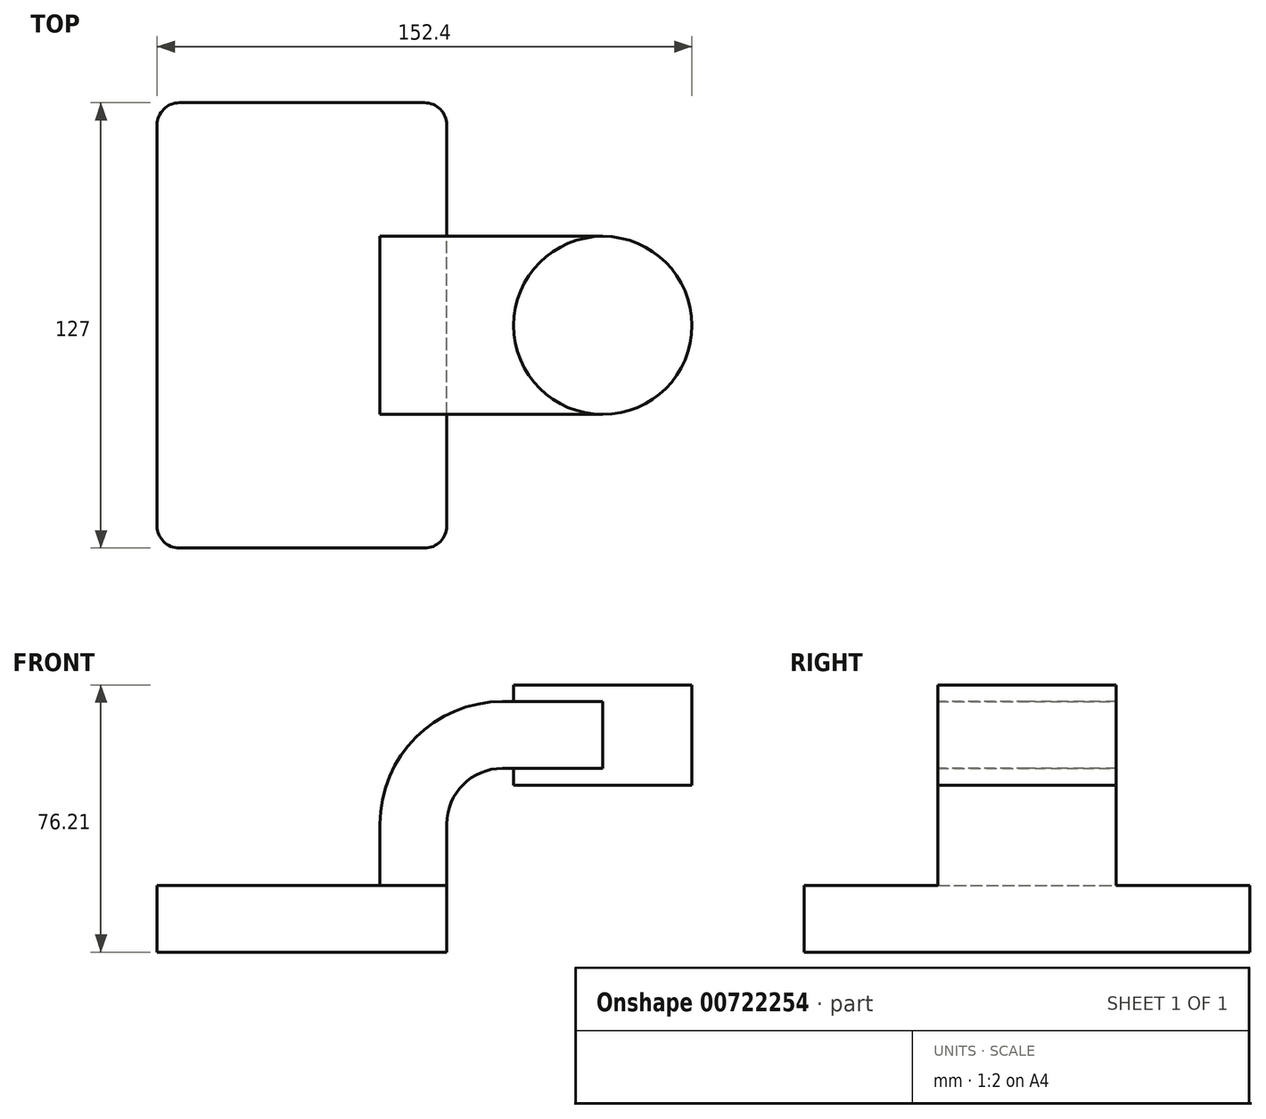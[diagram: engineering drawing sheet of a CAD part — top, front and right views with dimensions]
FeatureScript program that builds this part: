
annotation { "Feature Type Name" : "Feature", "Feature Type Description" : "" }
export const myFeature = defineFeature(function(context is Context, id is Id, definition is map)
    precondition{}
    {
        {
            var Q0;
            Q0=qCreatedBy(makeId("Front.planeOp"),FACE);
            var sketch = newSketch(context, id + "F0", { "sketchPlane" : qUnion([Q0])});
            skLineSegment(sketch, "E0.bottom", {"start": v(-41.28, 9.52) * mm, "end": v(41.28, 9.52) * mm});
            skLineSegment(sketch, "E0.top", {"start": v(-41.28, -9.52) * mm, "end": v(41.28, -9.52) * mm});
            skLineSegment(sketch, "E0.left", {"start": v(-41.28, 9.52) * mm, "end": v(-41.28, -9.52) * mm});
            skLineSegment(sketch, "E0.right", {"start": v(41.28, 9.52) * mm, "end": v(41.28, -9.52) * mm});
            skPoint(sketch, "E0.middle", {"position": v(0, 0) * mm});
            skLineSegment(sketch, "E1.bottom", {"start": v(111.13, 38.1) * mm, "end": v(60.33, 38.1) * mm});
            skLineSegment(sketch, "E1.top", {"start": v(111.13, 66.68) * mm, "end": v(60.33, 66.68) * mm});
            skLineSegment(sketch, "E1.left", {"start": v(111.13, 38.1) * mm, "end": v(111.13, 66.68) * mm});
            skLineSegment(sketch, "E1.right", {"start": v(60.33, 38.1) * mm, "end": v(60.33, 66.67) * mm});
            skPoint(sketch, "E1.middle", {"position": v(85.73, 52.39) * mm});
            skLineSegment(sketch, "E2", {"start": v(41.28, 9.52) * mm, "end": v(41.28, 27) * mm});
            skArc(sketch, "E3", {"start": v(41.28, 27) * mm, "mid": v(45.92, 38.23) * mm, "end": v(57.15, 42.88) * mm});
            skLineSegment(sketch, "E4", {"start": v(57.15, 42.88) * mm, "end": v(85.73, 42.88) * mm});
            skLineSegment(sketch, "E5.0", {"start": v(57.15, 61.93) * mm, "end": v(85.73, 61.93) * mm});
            skArc(sketch, "E5.1", {"start": v(22.23, 27) * mm, "mid": v(32.45, 51.7) * mm, "end": v(57.15, 61.93) * mm});
            skLineSegment(sketch, "E5.2", {"start": v(22.23, 9.52) * mm, "end": v(22.23, 27) * mm});
            skLineSegment(sketch, "E6", {"start": v(85.73, 38.1) * mm, "end": v(85.73, 66.68) * mm});
            skFitSpline(sketch, "E7", {"points": [v(-41.28, 9.53) * mm, v(57.15, 61.93) * mm], "startDerivative": vector(81.34, 68.93) * mm, "endDerivative": vector(97.24, -3.03) * mm});
            skSolve(sketch);
        }
        {
            var Q0;
            Q0=makeQuery(id+"F0.imprint","IMPRINT",FACE,{"disambiguationData":[TD([[makeQuery(id+"F0.imprint","IMPRINT",EDGE,{"derivedFrom":sQuery(id+"F0.wireOp",EDGE,"E0.top")}),1.0]])]});
            extrude(context, id + "F1", {"entities" : qUnion([Q0]), "endBound" : BoundingType.SYMMETRIC, "depth" : 127 * mm, "offsetDistance" : 25.4 * mm});
        }
        {
            var Q0;
            {var subQ1=sQuery(id+"F0.wireOp",EDGE,"E2");Q0=makeQuery(id+"F0.imprint","IMPRINT",FACE,{"disambiguationData":[TD([[makeQuery(id+"F0.imprint","IMPRINT",EDGE,{"derivedFrom":subQ1}),1.0]])]});}
            var Q1;
            {var subQ0=sQuery(id+"F0.wireOp",EDGE,"E4");var subQ1=sQuery(id+"F0.wireOp",EDGE,"E1.right");var subQ2=makeQuery(id+"F0.imprint","INTERSECT",VERTEX,{"derivedFrom":[subQ1,subQ0]});Q1=makeQuery(id+"F0.imprint","IMPRINT",FACE,{"disambiguationData":[TD([[makeQuery(id+"F0.imprint","IMPRINT",EDGE,{"disambiguationData":[TD([[subQ2,-1.0]])],"derivedFrom":subQ1}),-1.0]])]});}
            extrude(context, id + "F2", {"entities" : qUnion([Q0, Q1]), "operationType" : NewBodyOperationType.ADD, "endBound" : BoundingType.SYMMETRIC, "depth" : 50.8 * mm, "offsetDistance" : 25.4 * mm});
        }
        {
            var Q0;
            Q0=makeQuery(id+"F0.imprint","IMPRINT",FACE,{"disambiguationData":[TD([[makeQuery(id+"F0.imprint","IMPRINT",EDGE,{"derivedFrom":sQuery(id+"F0.wireOp",EDGE,"E5.1")}),1.0]])]});
            extrude(context, id + "F3", {"entities" : qUnion([Q0]), "operationType" : NewBodyOperationType.ADD, "depth" : 15.88 * mm, "offsetDistance" : 25.4 * mm});
        }
        {
            var Q0;
            {var subQ4=sQuery(id+"F0.wireOp",EDGE,"E1.left");Q0=makeQuery(id+"F0.imprint","IMPRINT",FACE,{"disambiguationData":[TD([[makeQuery(id+"F0.imprint","IMPRINT",EDGE,{"derivedFrom":subQ4}),1.0]])]});}
            var Q1;
            Q1=sQuery(id+"F0.wireOp",EDGE,"E6");
            revolve(context, id + "F4", {"operationType" : NewBodyOperationType.ADD, "surfaceOperationType" : NewSurfaceOperationType.NEW, "entities" : qUnion([Q0]), "axis" : qUnion([Q1]), "revolveType" : RevolveType.FULL});
        }
        {
            var Q0;
            Q0=makeQuery(id+"F1.opExtrude","CAP_EDGE",EDGE,{"disambiguationData":[OSD([sQuery(id+"F0.wireOp",EDGE,"E0.right")])],"isStart":false});
            var Q1;
            Q1=makeQuery(id+"F1.opExtrude","CAP_EDGE",EDGE,{"disambiguationData":[OSD([sQuery(id+"F0.wireOp",EDGE,"E0.left")])],"isStart":false});
            var Q2;
            Q2=makeQuery(id+"F1.opExtrude","CAP_EDGE",EDGE,{"disambiguationData":[OSD([sQuery(id+"F0.wireOp",EDGE,"E0.left")])],"isStart":true});
            var Q3;
            Q3=makeQuery(id+"F1.opExtrude","CAP_EDGE",EDGE,{"disambiguationData":[OSD([sQuery(id+"F0.wireOp",EDGE,"E0.right")])],"isStart":true});
            fillet(context, id + "F5", {"entities" : qUnion([Q0, Q1, Q2, Q3]), "radius" : 6.35 * mm, "tangentPropagation" : true, "allowEdgeOverflow" : false});
        }
    });
